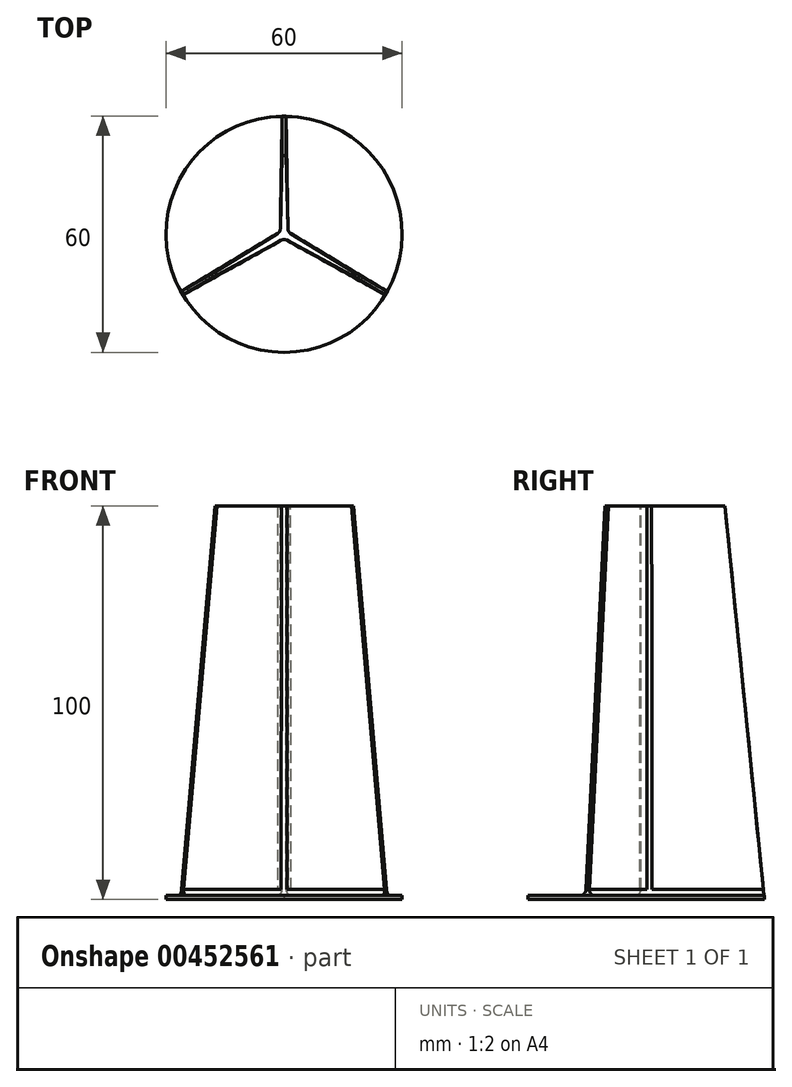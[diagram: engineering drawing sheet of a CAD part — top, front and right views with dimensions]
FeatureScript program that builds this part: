
annotation { "Feature Type Name" : "Feature", "Feature Type Description" : "" }
export const myFeature = defineFeature(function(context is Context, id is Id, definition is map)
    precondition{}
    {
        {
            assignVariable(context, id + "F0", {"variableType" : VariableType.LENGTH, "name" : "armLen", "lengthValue" : 100 * mm});
        }
        {
            var Q0;
            Q0=qCreatedBy(makeId("Top.planeOp"),FACE);
            var sketch = newSketch(context, id + "F1", { "sketchPlane" : qUnion([Q0])});
            skArc(sketch, "E0", {"start": v(-0.5, 30) * mm, "mid": v(0, -30) * mm, "end": v(0.5, 30) * mm});
            skLineSegment(sketch, "E1", {"start": v(0, 0) * mm, "end": v(1, 0) * mm});
            skLineSegment(sketch, "E2", {"start": v(0, 0) * mm, "end": v(0, 30) * mm, "construction": true});
            skLineSegment(sketch, "E3", {"start": v(0, 30) * mm, "end": v(0.5, 30) * mm});
            skLineSegment(sketch, "E4", {"start": v(0.5, 30) * mm, "end": v(1, 0) * mm});
            skLineSegment(sketch, "E5.MirrorCS", {"start": v(-0.5, 30) * mm, "end": v(-1, 0) * mm});
            skLineSegment(sketch, "E6.MirrorCS", {"start": v(0, 0) * mm, "end": v(-1, 0) * mm});
            skLineSegment(sketch, "E7.MirrorCS", {"start": v(0, 30) * mm, "end": v(-0.5, 30) * mm});
            skLineSegment(sketch, "E8.1.0", {"start": v(-26.23, -14.56) * mm, "end": v(-0.5, 0.87) * mm});
            skLineSegment(sketch, "E8.1.1", {"start": v(0, 0) * mm, "end": v(-0.5, 0.87) * mm});
            skLineSegment(sketch, "E8.1.2", {"start": v(0, 0) * mm, "end": v(0.5, -0.87) * mm});
            skLineSegment(sketch, "E8.1.3", {"start": v(-25.73, -15.43) * mm, "end": v(0.5, -0.87) * mm});
            skLineSegment(sketch, "E8.1.4", {"start": v(-25.98, -15) * mm, "end": v(-25.73, -15.43) * mm});
            skLineSegment(sketch, "E8.1.5", {"start": v(-25.98, -15) * mm, "end": v(-26.23, -14.56) * mm});
            skLineSegment(sketch, "E8.2.0", {"start": v(25.73, -15.43) * mm, "end": v(-0.5, -0.87) * mm});
            skLineSegment(sketch, "E8.2.1", {"start": v(0, 0) * mm, "end": v(-0.5, -0.87) * mm});
            skLineSegment(sketch, "E8.2.2", {"start": v(0, 0) * mm, "end": v(0.5, 0.87) * mm});
            skLineSegment(sketch, "E8.2.3", {"start": v(26.23, -14.56) * mm, "end": v(0.5, 0.87) * mm});
            skLineSegment(sketch, "E8.2.4", {"start": v(25.98, -15) * mm, "end": v(26.23, -14.56) * mm});
            skLineSegment(sketch, "E8.2.5", {"start": v(25.98, -15) * mm, "end": v(25.73, -15.43) * mm});
            skSolve(sketch);
        }
        {
            var Q0;
            Q0=qCreatedBy(makeId("Top.planeOp"),FACE);
            cPlane(context, id + "F2", {"entities" : qUnion([Q0]), "cplaneType" : CPlaneType.OFFSET, "offset" : getVariable(context, 'armLen'), "width" : 150 * mm, "height" : 150 * mm});
        }
        {
            var Q0;
            Q0=qCreatedBy(id+"F2.planeOp",FACE);
            var sketch = newSketch(context, id + "F3", { "sketchPlane" : qUnion([Q0])});
            skArc(sketch, "E9", {"start": v(-0.5, 20) * mm, "mid": v(0, -20) * mm, "end": v(0.5, 20) * mm});
            skLineSegment(sketch, "E10", {"start": v(0, 0) * mm, "end": v(1, 0) * mm});
            skLineSegment(sketch, "E11", {"start": v(0, 0) * mm, "end": v(0, 20) * mm, "construction": true});
            skLineSegment(sketch, "E12", {"start": v(0, 20) * mm, "end": v(0.5, 20) * mm});
            skLineSegment(sketch, "E13", {"start": v(0.5, 20) * mm, "end": v(1, 0) * mm});
            skLineSegment(sketch, "E14.MirrorCS", {"start": v(-0.5, 20) * mm, "end": v(-1, 0) * mm});
            skLineSegment(sketch, "E15.MirrorCS", {"start": v(0, 0) * mm, "end": v(-1, 0) * mm});
            skLineSegment(sketch, "E16.MirrorCS", {"start": v(0, 20) * mm, "end": v(-0.5, 20) * mm});
            skLineSegment(sketch, "E17.1.0", {"start": v(-17.57, -9.56) * mm, "end": v(-0.5, 0.87) * mm});
            skLineSegment(sketch, "E17.1.1", {"start": v(0, 0) * mm, "end": v(-0.5, 0.87) * mm});
            skLineSegment(sketch, "E17.1.2", {"start": v(0, 0) * mm, "end": v(0.5, -0.87) * mm});
            skLineSegment(sketch, "E17.1.3", {"start": v(-17.07, -10.43) * mm, "end": v(0.5, -0.87) * mm});
            skLineSegment(sketch, "E17.1.4", {"start": v(-17.32, -10) * mm, "end": v(-17.07, -10.43) * mm});
            skLineSegment(sketch, "E17.1.5", {"start": v(-17.32, -10) * mm, "end": v(-17.57, -9.56) * mm});
            skLineSegment(sketch, "E17.2.0", {"start": v(17.07, -10.43) * mm, "end": v(-0.5, -0.87) * mm});
            skLineSegment(sketch, "E17.2.1", {"start": v(0, 0) * mm, "end": v(-0.5, -0.87) * mm});
            skLineSegment(sketch, "E17.2.2", {"start": v(0, 0) * mm, "end": v(0.5, 0.87) * mm});
            skLineSegment(sketch, "E17.2.3", {"start": v(17.57, -9.56) * mm, "end": v(0.5, 0.87) * mm});
            skLineSegment(sketch, "E17.2.4", {"start": v(17.32, -10) * mm, "end": v(17.57, -9.56) * mm});
            skLineSegment(sketch, "E17.2.5", {"start": v(17.32, -10) * mm, "end": v(17.07, -10.43) * mm});
            skSolve(sketch);
        }
        {
            var Q0;
            {var subQ9=sQuery(id+"F3.wireOp",EDGE,"E15.MirrorCS");Q0=makeQuery(id+"F3.imprint","IMPRINT",FACE,{"disambiguationData":[TD([[makeQuery(id+"F3.imprint","IMPRINT",EDGE,{"derivedFrom":subQ9}),1.0]])]});}
            var Q1;
            {var subQ9=sQuery(id+"F1.wireOp",EDGE,"E6.MirrorCS");Q1=makeQuery(id+"F1.imprint","IMPRINT",FACE,{"disambiguationData":[TD([[makeQuery(id+"F1.imprint","IMPRINT",EDGE,{"derivedFrom":subQ9}),1.0]])]});}
            loft(context, id + "F4", {"sheetProfilesArray" : [{ "sheetProfileEntities" : qUnion([Q0]) }, { "sheetProfileEntities" : qUnion([Q1]) }]});
        }
        {
            var Q1;
            {var subQ0=sQuery(id+"F1.wireOp",EDGE,"E8.1.2");Q1=makeQuery(id+"F1.imprint","IMPRINT",FACE,{"disambiguationData":[TD([[makeQuery(id+"F1.imprint","IMPRINT",EDGE,{"derivedFrom":subQ0}),-1.0]])]});}
            var Q2;
            {var subQ0=sQuery(id+"F3.wireOp",EDGE,"E17.1.2");Q2=makeQuery(id+"F3.imprint","IMPRINT",FACE,{"disambiguationData":[TD([[makeQuery(id+"F3.imprint","IMPRINT",EDGE,{"derivedFrom":subQ0}),-1.0]])]});}
            loft(context, id + "F5", {"operationType" : NewBodyOperationType.ADD, "sheetProfilesArray" : [{ "sheetProfileEntities" : qUnion([Q1]) }, { "sheetProfileEntities" : qUnion([Q2]) }]});
        }
        {
            var Q1;
            {var subQ1=sQuery(id+"F1.wireOp",EDGE,"E1");Q1=makeQuery(id+"F1.imprint","IMPRINT",FACE,{"disambiguationData":[TD([[makeQuery(id+"F1.imprint","IMPRINT",EDGE,{"derivedFrom":subQ1}),-1.0]])]});}
            var Q2;
            {var subQ1=sQuery(id+"F3.wireOp",EDGE,"E10");Q2=makeQuery(id+"F3.imprint","IMPRINT",FACE,{"disambiguationData":[TD([[makeQuery(id+"F3.imprint","IMPRINT",EDGE,{"derivedFrom":subQ1}),-1.0]])]});}
            loft(context, id + "F6", {"operationType" : NewBodyOperationType.ADD, "sheetProfilesArray" : [{ "sheetProfileEntities" : qUnion([Q1]) }, { "sheetProfileEntities" : qUnion([Q2]) }]});
        }
        {
            var Q1;
            {var subQ0=sQuery(id+"F1.wireOp",EDGE,"E1");Q1=makeQuery(id+"F1.imprint","IMPRINT",FACE,{"disambiguationData":[TD([[makeQuery(id+"F1.imprint","IMPRINT",EDGE,{"derivedFrom":subQ0}),1.0]])]});}
            var Q2;
            {var subQ0=sQuery(id+"F3.wireOp",EDGE,"E10");Q2=makeQuery(id+"F3.imprint","IMPRINT",FACE,{"disambiguationData":[TD([[makeQuery(id+"F3.imprint","IMPRINT",EDGE,{"derivedFrom":subQ0}),1.0]])]});}
            loft(context, id + "F7", {"operationType" : NewBodyOperationType.ADD, "sheetProfilesArray" : [{ "sheetProfileEntities" : qUnion([Q1]) }, { "sheetProfileEntities" : qUnion([Q2]) }]});
        }
        {
            var Q1;
            {var subQ0=sQuery(id+"F1.wireOp",EDGE,"E6.MirrorCS");Q1=makeQuery(id+"F1.imprint","IMPRINT",FACE,{"disambiguationData":[TD([[makeQuery(id+"F1.imprint","IMPRINT",EDGE,{"derivedFrom":subQ0}),-1.0]])]});}
            var Q2;
            {var subQ0=sQuery(id+"F3.wireOp",EDGE,"E15.MirrorCS");Q2=makeQuery(id+"F3.imprint","IMPRINT",FACE,{"disambiguationData":[TD([[makeQuery(id+"F3.imprint","IMPRINT",EDGE,{"derivedFrom":subQ0}),-1.0]])]});}
            loft(context, id + "F8", {"operationType" : NewBodyOperationType.ADD, "sheetProfilesArray" : [{ "sheetProfileEntities" : qUnion([Q1]) }, { "sheetProfileEntities" : qUnion([Q2]) }]});
        }
        {
            var Q1;
            {var subQ6=sQuery(id+"F1.wireOp",EDGE,"E3");Q1=makeQuery(id+"F1.imprint","IMPRINT",FACE,{"disambiguationData":[TD([[makeQuery(id+"F1.imprint","IMPRINT",EDGE,{"derivedFrom":subQ6}),-1.0]])]});}
            var Q2;
            {var subQ6=sQuery(id+"F3.wireOp",EDGE,"E12");Q2=makeQuery(id+"F3.imprint","IMPRINT",FACE,{"disambiguationData":[TD([[makeQuery(id+"F3.imprint","IMPRINT",EDGE,{"derivedFrom":subQ6}),-1.0]])]});}
            loft(context, id + "F9", {"operationType" : NewBodyOperationType.ADD, "sheetProfilesArray" : [{ "sheetProfileEntities" : qUnion([Q1]) }, { "sheetProfileEntities" : qUnion([Q2]) }]});
        }
        {
            var Q0;
            Q0 = qSketchRegion(id + "F1", true);
            var Q1;
            {var subQ0=sQuery(id+"F1.wireOp",EDGE,"E6.MirrorCS");Q1=makeQuery(id+"F1.imprint","IMPRINT",FACE,{"disambiguationData":[TD([[makeQuery(id+"F1.imprint","IMPRINT",EDGE,{"derivedFrom":subQ0}),-1.0]])]});}
            var Q2;
            {var subQ0=sQuery(id+"F1.wireOp",EDGE,"E1");Q2=makeQuery(id+"F1.imprint","IMPRINT",FACE,{"disambiguationData":[TD([[makeQuery(id+"F1.imprint","IMPRINT",EDGE,{"derivedFrom":subQ0}),1.0]])]});}
            var Q3;
            {var subQ0=sQuery(id+"F1.wireOp",EDGE,"E8.1.2");Q3=makeQuery(id+"F1.imprint","IMPRINT",FACE,{"disambiguationData":[TD([[makeQuery(id+"F1.imprint","IMPRINT",EDGE,{"derivedFrom":subQ0}),-1.0]])]});}
            extrude(context, id + "F10", {"entities" : qUnion([Q0, Q1, Q2, Q3]), "operationType" : NewBodyOperationType.ADD, "depth" : 1 * mm, "offsetDistance" : 25 * mm});
        }
        {
            var Q0;
            {var subQ0=sQuery(id+"F1.wireOp",EDGE,"E0");Q0=makeQuery(id+"F10.boolean.opBoolean","INTERSECT",EDGE,{"derivedFrom":[makeQuery(id+"F6.opLoft","SWEPT_FACE",FACE,{"disambiguationData":[OSD([subQ0,sQuery(id+"F1.wireOp",EDGE,"E8.1.3"),sQuery(id+"F1.wireOp",EDGE,"E8.2.0"),sQuery(id+"F1.wireOp",EDGE,"E8.2.5"),sQuery(id+"F3.wireOp",EDGE,"E9"),sQuery(id+"F3.wireOp",EDGE,"E17.1.3"),sQuery(id+"F3.wireOp",EDGE,"E17.2.0"),sQuery(id+"F3.wireOp",EDGE,"E17.2.5")])]}),makeQuery(id+"F10.opExtrude","CAP_FACE",FACE,{"disambiguationData":[OSD([subQ0,sQuery(id+"F1.wireOp",EDGE,"E3"),sQuery(id+"F1.wireOp",EDGE,"E7.MirrorCS")])],"isStart":false})]});}
            var Q1;
            {var subQ0=sQuery(id+"F1.wireOp",EDGE,"E0");Q1=makeQuery(id+"F10.boolean.opBoolean","INTERSECT",EDGE,{"derivedFrom":[makeQuery(id+"F4.opLoft","SWEPT_FACE",FACE,{"disambiguationData":[OSD([subQ0,sQuery(id+"F1.wireOp",EDGE,"E8.1.3"),sQuery(id+"F1.wireOp",EDGE,"E8.1.4"),sQuery(id+"F1.wireOp",EDGE,"E8.2.0"),sQuery(id+"F3.wireOp",EDGE,"E9"),sQuery(id+"F3.wireOp",EDGE,"E17.1.3"),sQuery(id+"F3.wireOp",EDGE,"E17.1.4"),sQuery(id+"F3.wireOp",EDGE,"E17.2.0")])]}),makeQuery(id+"F10.opExtrude","CAP_FACE",FACE,{"disambiguationData":[OSD([subQ0,sQuery(id+"F1.wireOp",EDGE,"E3"),sQuery(id+"F1.wireOp",EDGE,"E7.MirrorCS")])],"isStart":false})]});}
            var Q2;
            {var subQ0=sQuery(id+"F1.wireOp",EDGE,"E0");Q2=makeQuery(id+"F10.boolean.opBoolean","INTERSECT",EDGE,{"derivedFrom":[makeQuery(id+"F6.opLoft","SWEPT_FACE",FACE,{"disambiguationData":[OSD([subQ0,sQuery(id+"F1.wireOp",EDGE,"E4"),sQuery(id+"F1.wireOp",EDGE,"E8.2.3"),sQuery(id+"F1.wireOp",EDGE,"E8.2.4"),sQuery(id+"F3.wireOp",EDGE,"E9"),sQuery(id+"F3.wireOp",EDGE,"E13"),sQuery(id+"F3.wireOp",EDGE,"E17.2.3"),sQuery(id+"F3.wireOp",EDGE,"E17.2.4")])]}),makeQuery(id+"F10.opExtrude","CAP_FACE",FACE,{"disambiguationData":[OSD([subQ0,sQuery(id+"F1.wireOp",EDGE,"E3"),sQuery(id+"F1.wireOp",EDGE,"E7.MirrorCS")])],"isStart":false})]});}
            var Q3;
            {var subQ0=sQuery(id+"F1.wireOp",EDGE,"E3");var subQ1=sQuery(id+"F1.wireOp",EDGE,"E0");Q3=makeQuery(id+"F10.boolean.opBoolean","INTERSECT",EDGE,{"derivedFrom":[makeQuery(id+"F9.opLoft","SWEPT_FACE",FACE,{"disambiguationData":[OSD([subQ1,subQ0,sQuery(id+"F1.wireOp",EDGE,"E4"),sQuery(id+"F1.wireOp",EDGE,"E8.2.3"),sQuery(id+"F3.wireOp",EDGE,"E9"),sQuery(id+"F3.wireOp",EDGE,"E12"),sQuery(id+"F3.wireOp",EDGE,"E13"),sQuery(id+"F3.wireOp",EDGE,"E17.2.3")])]}),makeQuery(id+"F10.opExtrude","CAP_FACE",FACE,{"disambiguationData":[OSD([subQ1,subQ0,sQuery(id+"F1.wireOp",EDGE,"E7.MirrorCS")])],"isStart":false})]});}
            var Q4;
            {var subQ0=sQuery(id+"F1.wireOp",EDGE,"E7.MirrorCS");var subQ1=sQuery(id+"F1.wireOp",EDGE,"E0");Q4=makeQuery(id+"F10.boolean.opBoolean","INTERSECT",EDGE,{"derivedFrom":[makeQuery(id+"F9.opLoft","SWEPT_FACE",FACE,{"disambiguationData":[OSD([subQ1,sQuery(id+"F1.wireOp",EDGE,"E5.MirrorCS"),subQ0,sQuery(id+"F1.wireOp",EDGE,"E8.1.0"),sQuery(id+"F3.wireOp",EDGE,"E9"),sQuery(id+"F3.wireOp",EDGE,"E14.MirrorCS"),sQuery(id+"F3.wireOp",EDGE,"E16.MirrorCS"),sQuery(id+"F3.wireOp",EDGE,"E17.1.0")])]}),makeQuery(id+"F10.opExtrude","CAP_FACE",FACE,{"disambiguationData":[OSD([subQ1,sQuery(id+"F1.wireOp",EDGE,"E3"),subQ0])],"isStart":false})]});}
            var Q5;
            {var subQ0=sQuery(id+"F1.wireOp",EDGE,"E0");Q5=makeQuery(id+"F10.boolean.opBoolean","INTERSECT",EDGE,{"derivedFrom":[makeQuery(id+"F4.opLoft","SWEPT_FACE",FACE,{"disambiguationData":[OSD([subQ0,sQuery(id+"F1.wireOp",EDGE,"E5.MirrorCS"),sQuery(id+"F1.wireOp",EDGE,"E8.1.0"),sQuery(id+"F1.wireOp",EDGE,"E8.1.5"),sQuery(id+"F3.wireOp",EDGE,"E9"),sQuery(id+"F3.wireOp",EDGE,"E14.MirrorCS"),sQuery(id+"F3.wireOp",EDGE,"E17.1.0"),sQuery(id+"F3.wireOp",EDGE,"E17.1.5")])]}),makeQuery(id+"F10.opExtrude","CAP_FACE",FACE,{"disambiguationData":[OSD([subQ0,sQuery(id+"F1.wireOp",EDGE,"E3"),sQuery(id+"F1.wireOp",EDGE,"E7.MirrorCS")])],"isStart":false})]});}
            var Q6;
            {var subQ0=sQuery(id+"F3.wireOp",EDGE,"E17.2.3");var subQ1=sQuery(id+"F3.wireOp",EDGE,"E13");var subQ2=sQuery(id+"F1.wireOp",EDGE,"E8.2.3");var subQ3=sQuery(id+"F1.wireOp",EDGE,"E4");Q6=makeQuery(id+"F9.boolean.opBoolean","MERGE",EDGE,{"derivedFrom":[makeQuery(id+"F7.boolean.opBoolean","MERGE",EDGE,{"derivedFrom":[makeQuery(id+"F6.opLoft","SWEPT_EDGE",EDGE,{"disambiguationData":[OSD([subQ3,subQ2,subQ1,subQ0])]}),makeQuery(id+"F7.opLoft","SWEPT_EDGE",EDGE,{"disambiguationData":[OSD([subQ3,subQ2,subQ1,subQ0])]})]}),makeQuery(id+"F9.opLoft","SWEPT_EDGE",EDGE,{"disambiguationData":[OSD([subQ3,subQ2,subQ1,subQ0])]})]});}
            var Q7;
            {var subQ0=sQuery(id+"F3.wireOp",EDGE,"E17.1.0");var subQ1=sQuery(id+"F3.wireOp",EDGE,"E14.MirrorCS");var subQ2=sQuery(id+"F1.wireOp",EDGE,"E8.1.0");var subQ3=sQuery(id+"F1.wireOp",EDGE,"E5.MirrorCS");Q7=makeQuery(id+"F9.boolean.opBoolean","MERGE",EDGE,{"derivedFrom":[makeQuery(id+"F8.boolean.opBoolean","MERGE",EDGE,{"derivedFrom":[makeQuery(id+"F4.opLoft","SWEPT_EDGE",EDGE,{"disambiguationData":[OSD([subQ3,subQ2,subQ1,subQ0])]}),makeQuery(id+"F8.opLoft","SWEPT_EDGE",EDGE,{"disambiguationData":[OSD([subQ3,subQ2,subQ1,subQ0])]})]}),makeQuery(id+"F9.opLoft","SWEPT_EDGE",EDGE,{"disambiguationData":[OSD([subQ3,subQ2,subQ1,subQ0])]})]});}
            var Q8;
            {var subQ0=sQuery(id+"F3.wireOp",EDGE,"E17.2.0");var subQ1=sQuery(id+"F3.wireOp",EDGE,"E17.1.3");var subQ2=sQuery(id+"F1.wireOp",EDGE,"E8.2.0");var subQ3=sQuery(id+"F1.wireOp",EDGE,"E8.1.3");Q8=makeQuery(id+"F6.boolean.opBoolean","MERGE",EDGE,{"derivedFrom":[makeQuery(id+"F5.boolean.opBoolean","MERGE",EDGE,{"derivedFrom":[makeQuery(id+"F4.opLoft","SWEPT_EDGE",EDGE,{"disambiguationData":[OSD([subQ3,subQ2,subQ1,subQ0])]}),makeQuery(id+"F5.opLoft","SWEPT_EDGE",EDGE,{"disambiguationData":[OSD([subQ3,subQ2,subQ1,subQ0])]})]}),makeQuery(id+"F6.opLoft","SWEPT_EDGE",EDGE,{"disambiguationData":[OSD([subQ3,subQ2,subQ1,subQ0])]})]});}
            fillet(context, id + "F11", {"entities" : qUnion([Q0, Q1, Q2, Q3, Q4, Q5, Q6, Q7, Q8]), "radius" : 1.5 * mm, "tangentPropagation" : true, "allowEdgeOverflow" : false});
        }
    });
